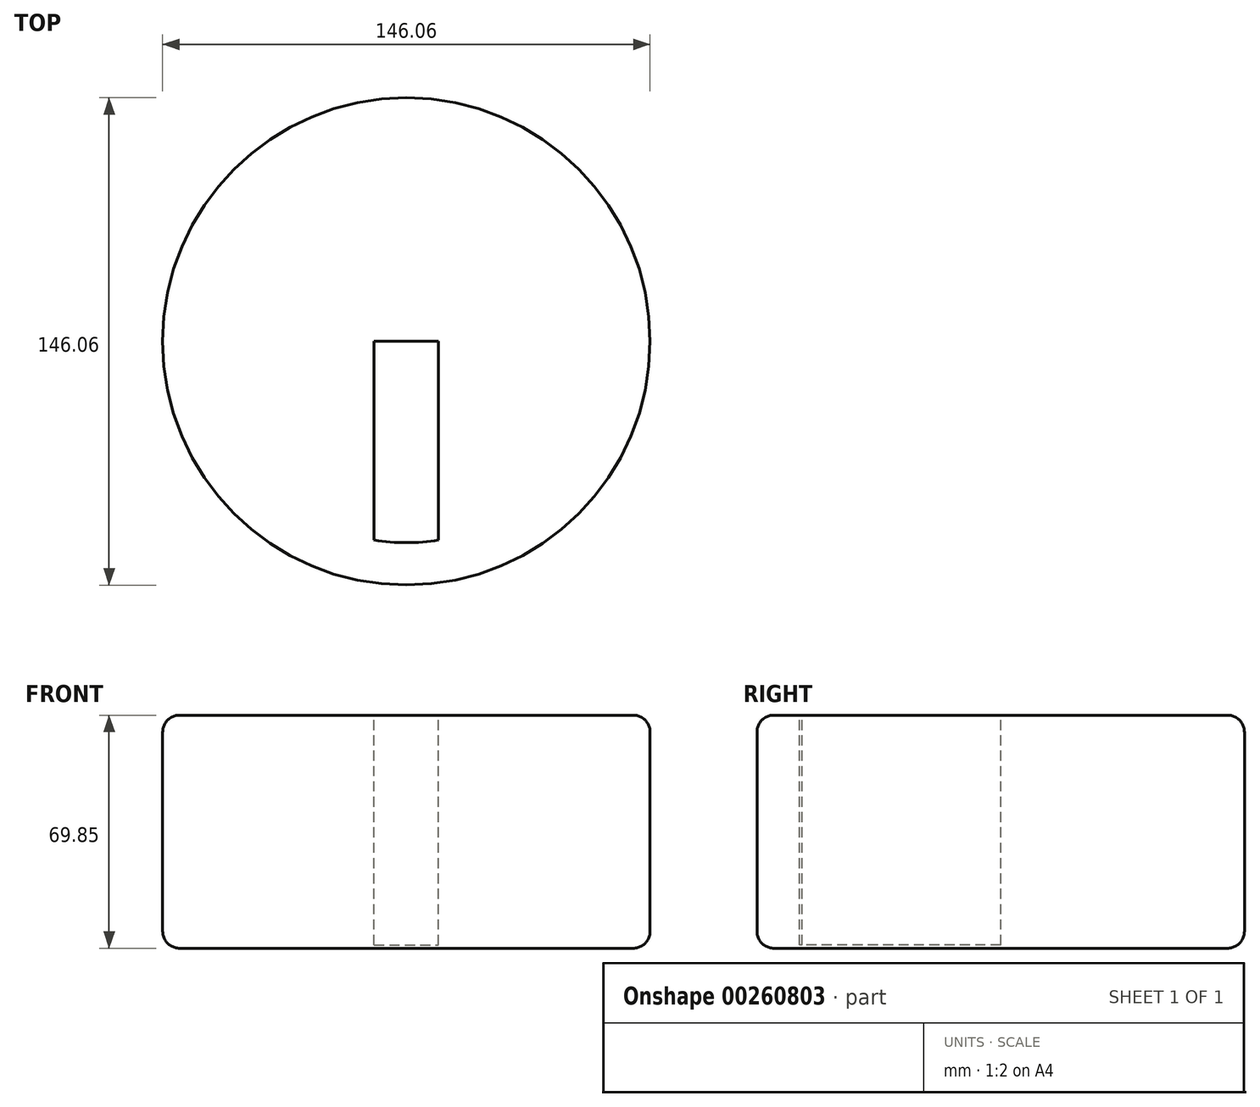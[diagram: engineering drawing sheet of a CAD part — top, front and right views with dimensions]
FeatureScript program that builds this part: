
annotation { "Feature Type Name" : "Feature", "Feature Type Description" : "" }
export const myFeature = defineFeature(function(context is Context, id is Id, definition is map)
    precondition{}
    {
        {
            var Q0;
            Q0=qCreatedBy(makeId("Top.planeOp"),FACE);
            var sketch = newSketch(context, id + "F0", { "sketchPlane" : qUnion([Q0])});
            skCircle(sketch, "E0", {"center": v(0, 0) * mm, "radius": 73.03 * mm});
            skSolve(sketch);
        }
        {
            var Q0;
            Q0 = qSketchRegion(id + "F0", true);
            extrude(context, id + "F1", {"entities" : qUnion([Q0]), "depth" : 69.85 * mm});
        }
        {
            var Q0;
            Q0=makeQuery(id+"F1.opExtrude","CAP_FACE",FACE,{"disambiguationData":[OSD([sQuery(id+"F0.wireOp",EDGE,"E0")])],"isStart":false});
            var sketch = newSketch(context, id + "F2", { "sketchPlane" : qUnion([Q0])});
            skCircle(sketch, "E1", {"center": v(0, 0) * mm, "radius": 60.33 * mm});
            skLineSegment(sketch, "E2", {"start": v(-9.65, 0) * mm, "end": v(9.65, 0) * mm});
            skLineSegment(sketch, "E3", {"start": v(-9.65, 0) * mm, "end": v(-9.65, 59.55) * mm});
            skLineSegment(sketch, "E4", {"start": v(-9.65, 59.55) * mm, "end": v(-9.65, -59.55) * mm});
            skLineSegment(sketch, "E5", {"start": v(9.65, 0) * mm, "end": v(9.65, 59.55) * mm});
            skLineSegment(sketch, "E6", {"start": v(9.65, 59.55) * mm, "end": v(9.65, -59.55) * mm});
            skSolve(sketch);
        }
        {
            var Q0;
            {var subQ0=sQuery(id+"F2.wireOp",EDGE,"E4");var subQ1=sQuery(id+"F2.wireOp",EDGE,"E1");var subQ2=makeQuery(id+"F2.imprint","INTERSECT",VERTEX,{"disambiguationData":[OD(0.0)],"derivedFrom":[subQ1,subQ0]});Q0=makeQuery(id+"F2.imprint","IMPRINT",FACE,{"disambiguationData":[TD([[makeQuery(id+"F2.imprint","IMPRINT",EDGE,{"disambiguationData":[TD([[subQ2,-1.0]])],"derivedFrom":subQ1}),1.0]])]});}
            var Q1;
            {var subQ0=sQuery(id+"F2.wireOp",EDGE,"E6");var subQ1=sQuery(id+"F2.wireOp",EDGE,"E1");var subQ2=makeQuery(id+"F2.imprint","INTERSECT",VERTEX,{"disambiguationData":[OD(0.0)],"derivedFrom":[subQ1,subQ0]});Q1=makeQuery(id+"F2.imprint","IMPRINT",FACE,{"disambiguationData":[TD([[makeQuery(id+"F2.imprint","IMPRINT",EDGE,{"disambiguationData":[TD([[subQ2,1.0]])],"derivedFrom":subQ1}),1.0]])]});}
            extrude(context, id + "F3", {"entities" : qUnion([Q0, Q1]), "operationType" : NewBodyOperationType.REMOVE, "oppositeDirection" : true, "depth" : 68.83 * mm});
        }
        {
            var Q0;
            Q0=makeQuery(id+"F1.opExtrude","CAP_EDGE",EDGE,{"disambiguationData":[OSD([sQuery(id+"F0.wireOp",EDGE,"E0")])],"isStart":false});
            var Q1;
            Q1=makeQuery(id+"F3.boolean.opBoolean","COPY",EDGE,{"derivedFrom":makeQuery(id+"F3.opExtrude","CAP_EDGE",EDGE,{"disambiguationData":[OSD([sQuery(id+"F2.wireOp",EDGE,"E6")])],"isStart":true})});
            var Q2;
            {var subQ0=sQuery(id+"F2.wireOp",EDGE,"E6");var subQ1=sQuery(id+"F2.wireOp",EDGE,"E1");Q2=makeQuery(id+"F3.boolean.opBoolean","COPY",EDGE,{"derivedFrom":makeQuery(id+"F3.opExtrude","CAP_EDGE",EDGE,{"disambiguationData":[OSD([subQ1]),TDD([makeQuery(id+"F2.imprint","IMPRINT",EDGE,{"disambiguationData":[TD([[makeQuery(id+"F2.imprint","INTERSECT",VERTEX,{"disambiguationData":[OD(0.0)],"derivedFrom":[subQ1,subQ0]}),1.0]])],"derivedFrom":subQ1})])],"isStart":true})});}
            var Q3;
            Q3=makeQuery(id+"F3.boolean.opBoolean","COPY",EDGE,{"derivedFrom":makeQuery(id+"F3.opExtrude","CAP_EDGE",EDGE,{"disambiguationData":[OSD([sQuery(id+"F2.wireOp",EDGE,"E4")])],"isStart":true})});
            var Q4;
            {var subQ0=sQuery(id+"F2.wireOp",EDGE,"E4");var subQ1=sQuery(id+"F2.wireOp",EDGE,"E1");Q4=makeQuery(id+"F3.boolean.opBoolean","COPY",EDGE,{"derivedFrom":makeQuery(id+"F3.opExtrude","CAP_EDGE",EDGE,{"disambiguationData":[OSD([subQ1]),TDD([makeQuery(id+"F2.imprint","IMPRINT",EDGE,{"disambiguationData":[TD([[makeQuery(id+"F2.imprint","INTERSECT",VERTEX,{"disambiguationData":[OD(0.0)],"derivedFrom":[subQ1,subQ0]}),-1.0]])],"derivedFrom":subQ1})])],"isStart":true})});}
            var Q5;
            Q5=makeQuery(id+"F1.opExtrude","CAP_EDGE",EDGE,{"disambiguationData":[OSD([sQuery(id+"F0.wireOp",EDGE,"E0")])],"isStart":true});
            fillet(context, id + "F4", {"entities" : qUnion([Q0, Q1, Q2, Q3, Q4, Q5]), "radius" : 5.08 * mm, "tangentPropagation" : true, "allowEdgeOverflow" : false});
        }
    });
